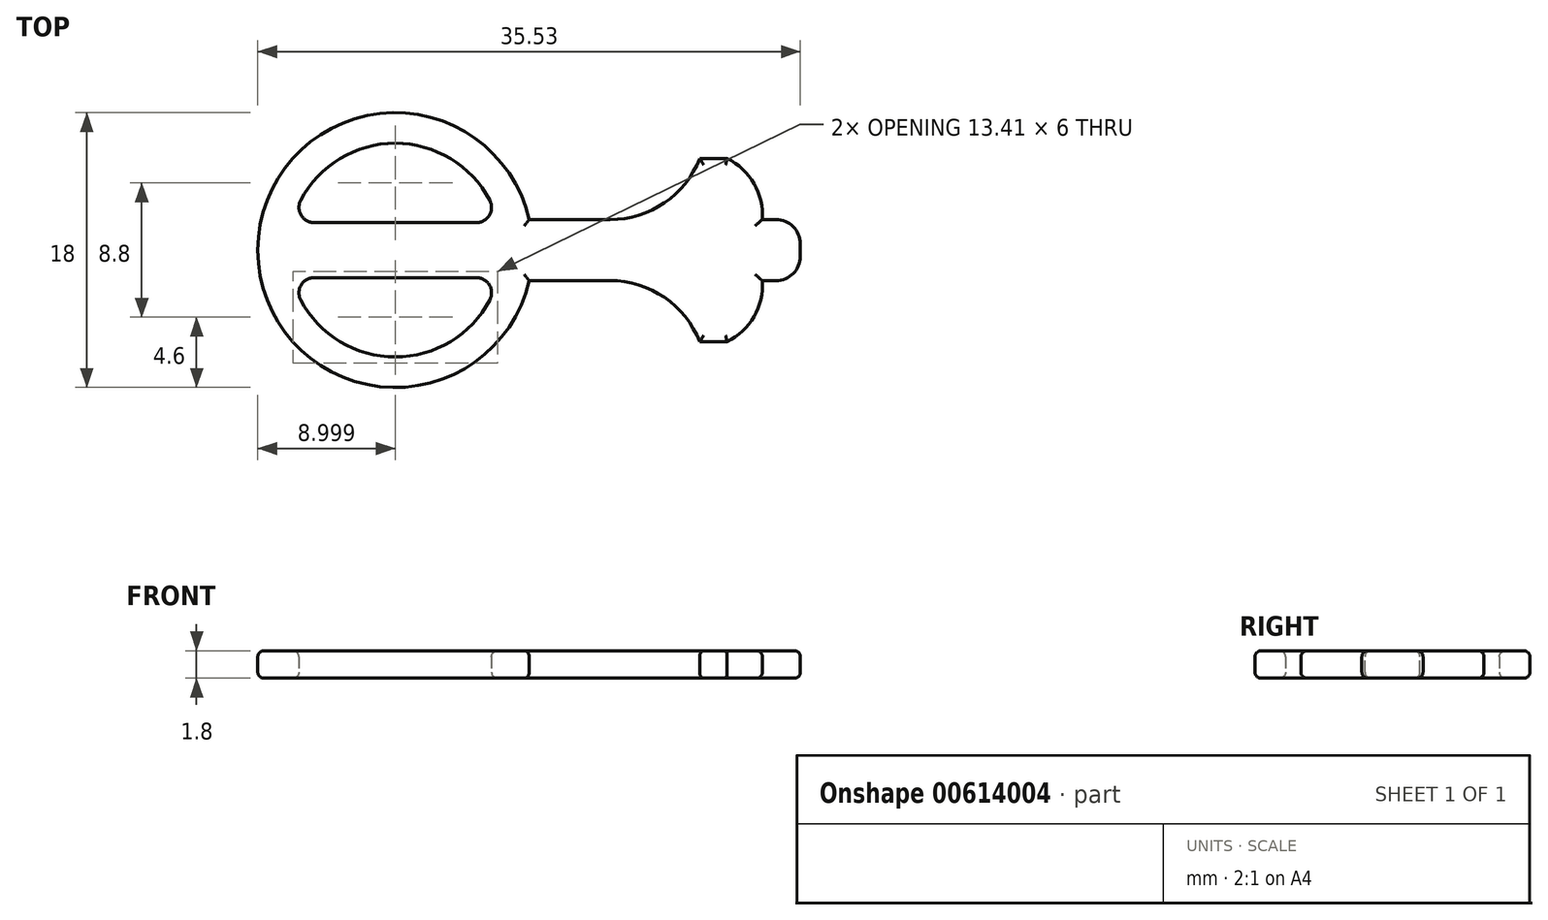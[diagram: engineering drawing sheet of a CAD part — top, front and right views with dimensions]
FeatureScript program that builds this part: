
annotation { "Feature Type Name" : "Feature", "Feature Type Description" : "" }
export const myFeature = defineFeature(function(context is Context, id is Id, definition is map)
    precondition{}
    {
        {
            var Q0;
            Q0=qCreatedBy(makeId("Top.planeOp"),FACE);
            var sketch = newSketch(context, id + "F0", { "sketchPlane" : qUnion([Q0])});
            skLineSegment(sketch, "E0", {"start": v(-11.78, 0) * mm, "end": v(23.75, 0) * mm});
            skLineSegment(sketch, "E1", {"start": v(23.75, 0) * mm, "end": v(23.75, -2) * mm});
            skLineSegment(sketch, "E2", {"start": v(23.75, -2) * mm, "end": v(21.25, -2) * mm});
            skArc(sketch, "E3", {"start": v(18.95, -6) * mm, "mid": v(20.72, -4.36) * mm, "end": v(21.25, -2) * mm});
            skLineSegment(sketch, "E4", {"start": v(18.95, -6) * mm, "end": v(17.15, -6) * mm});
            skArc(sketch, "E5", {"start": v(17.15, -6) * mm, "mid": v(14.84, -3.1) * mm, "end": v(11.3, -2) * mm});
            skPoint(sketch, "E5.endSnap0", {"position": v(22.5, -2) * mm});
            skArc(sketch, "E6", {"start": v(-11.78, 0) * mm, "mid": v(-3.79, -8.94) * mm, "end": v(6, -2) * mm});
            skLineSegment(sketch, "E7", {"start": v(-11.78, 0) * mm, "end": v(-11.78, 8.26) * mm, "construction": true});
            skArc(sketch, "E8.0", {"start": v(-9.55, -1.8) * mm, "mid": v(-2.78, -7) * mm, "end": v(3.98, -1.8) * mm});
            skLineSegment(sketch, "E9", {"start": v(3.98, -1.8) * mm, "end": v(-9.55, -1.8) * mm});
            skLineSegment(sketch, "E10", {"start": v(6, -2) * mm, "end": v(11.3, -2) * mm});
            skSolve(sketch);
        }
        {
            var Q0;
            {var subQ0=sQuery(id+"F0.wireOp",EDGE,"E3");Q0=makeQuery(id+"F0.imprint","IMPRINT",FACE,{"disambiguationData":[TD([[makeQuery(id+"F0.imprint","IMPRINT",EDGE,{"derivedFrom":subQ0}),1.0]])]});}
            var Q1;
            {var subQ7=sQuery(id+"F0.wireOp",EDGE,"E0");Q1=makeQuery(id+"F0.imprint","IMPRINT",FACE,{"disambiguationData":[TD([[makeQuery(id+"F0.imprint","IMPRINT",EDGE,{"derivedFrom":subQ7}),-1.0]])]});}
            var Q2;
            {var subQ3=sQuery(id+"F0.wireOp",EDGE,"E8.0");Q2=makeQuery(id+"F0.imprint","IMPRINT",FACE,{"disambiguationData":[TD([[makeQuery(id+"F0.imprint","IMPRINT",EDGE,{"derivedFrom":subQ3}),-1.0]])]});}
            extrude(context, id + "F1", {"entities" : qUnion([Q0, Q1, Q2]), "depth" : 1.8 * mm, "offsetDistance" : 25 * mm});
        }
        {
            var Q0;
            {var subQ0=sQuery(id+"F0.wireOp",EDGE,"E9");var subQ1=sQuery(id+"F0.wireOp",EDGE,"E8.0");Q0=makeQuery(id+"F1.opExtrude","SWEPT_EDGE",EDGE,{"disambiguationData":[OSD([subQ1,subQ0]),TDD([makeQuery(id+"F0.imprint","INTERSECT",VERTEX,{"disambiguationData":[OD(1.0)],"derivedFrom":[subQ1,subQ0]})])]});}
            var Q1;
            {var subQ0=sQuery(id+"F0.wireOp",EDGE,"E9");var subQ1=sQuery(id+"F0.wireOp",EDGE,"E8.0");Q1=makeQuery(id+"F1.opExtrude","SWEPT_EDGE",EDGE,{"disambiguationData":[OSD([subQ1,subQ0]),TDD([makeQuery(id+"F0.imprint","INTERSECT",VERTEX,{"disambiguationData":[OD(0.0)],"derivedFrom":[subQ1,subQ0]})])]});}
            fillet(context, id + "F2", {"entities" : qUnion([Q0, Q1]), "radius" : 1 * mm, "tangentPropagation" : true, "allowEdgeOverflow" : false});
        }
        {
            var Q0;
            Q0=makeQuery(id+"F1.opExtrude","SWEPT_BODY",BODY,{"disambiguationData":[OSD([sQuery(id+"F0.wireOp",EDGE,"E0"),sQuery(id+"F0.wireOp",EDGE,"E1"),sQuery(id+"F0.wireOp",EDGE,"E2"),sQuery(id+"F0.wireOp",EDGE,"E3"),sQuery(id+"F0.wireOp",EDGE,"E4"),sQuery(id+"F0.wireOp",EDGE,"E5"),sQuery(id+"F0.wireOp",EDGE,"G9BWcD3K-Wu3q-OJYY-iGBn-tdzcNZMlixlO"),sQuery(id+"F0.wireOp",EDGE,"E6"),sQuery(id+"F0.wireOp",EDGE,"E8.0"),sQuery(id+"F0.wireOp",EDGE,"OksKjaqa-pKnn-B38g-xFtQ-Ep9EwtVI3ODa")])]});
            var Q1;
            Q1=makeQuery(id+"F1.opExtrude","SWEPT_FACE",FACE,{"disambiguationData":[OSD([sQuery(id+"F0.wireOp",EDGE,"E0")])]});
            mirror(context, id + "F3", {"operationType" : NewBodyOperationType.ADD, "entities" : qUnion([Q0]), "mirrorPlane" : qUnion([Q1])});
        }
        {
            var Q0;
            Q0=makeQuery(id+"F1.opExtrude","CAP_FACE",FACE,{"disambiguationData":[OSD([sQuery(id+"F0.wireOp",EDGE,"E0"),sQuery(id+"F0.wireOp",EDGE,"E1"),sQuery(id+"F0.wireOp",EDGE,"E2"),sQuery(id+"F0.wireOp",EDGE,"E3"),sQuery(id+"F0.wireOp",EDGE,"E4"),sQuery(id+"F0.wireOp",EDGE,"E5"),sQuery(id+"F0.wireOp",EDGE,"G9BWcD3K-Wu3q-OJYY-iGBn-tdzcNZMlixlO"),sQuery(id+"F0.wireOp",EDGE,"E6"),sQuery(id+"F0.wireOp",EDGE,"E8.0"),sQuery(id+"F0.wireOp",EDGE,"OksKjaqa-pKnn-B38g-xFtQ-Ep9EwtVI3ODa")])],"isStart":false});
            var Q1;
            Q1=makeQuery(id+"F1.opExtrude","CAP_FACE",FACE,{"disambiguationData":[OSD([sQuery(id+"F0.wireOp",EDGE,"E0"),sQuery(id+"F0.wireOp",EDGE,"E1"),sQuery(id+"F0.wireOp",EDGE,"E2"),sQuery(id+"F0.wireOp",EDGE,"E3"),sQuery(id+"F0.wireOp",EDGE,"E4"),sQuery(id+"F0.wireOp",EDGE,"E5"),sQuery(id+"F0.wireOp",EDGE,"G9BWcD3K-Wu3q-OJYY-iGBn-tdzcNZMlixlO"),sQuery(id+"F0.wireOp",EDGE,"E6"),sQuery(id+"F0.wireOp",EDGE,"E8.0"),sQuery(id+"F0.wireOp",EDGE,"OksKjaqa-pKnn-B38g-xFtQ-Ep9EwtVI3ODa")])],"isStart":true});
            fillet(context, id + "F4", {"entities" : qUnion([Q0, Q1]), "radius" : 0.4 * mm, "tangentPropagation" : true, "allowEdgeOverflow" : false});
        }
        {
            var Q0;
            Q0=makeQuery(id+"F1.opExtrude","SWEPT_EDGE",EDGE,{"disambiguationData":[OSD([sQuery(id+"F0.wireOp",EDGE,"E1"),sQuery(id+"F0.wireOp",EDGE,"E2")])]});
            var Q1;
            Q1=makeQuery(id+"F3.opPattern","COPY",EDGE,{"derivedFrom":makeQuery(id+"F1.opExtrude","SWEPT_EDGE",EDGE,{"disambiguationData":[OSD([sQuery(id+"F0.wireOp",EDGE,"E1"),sQuery(id+"F0.wireOp",EDGE,"E2")])]}),"instanceName":"1"});
            fillet(context, id + "F5", {"entities" : qUnion([Q0, Q1]), "radius" : 1.6 * mm, "tangentPropagation" : true, "allowEdgeOverflow" : false});
        }
    });
